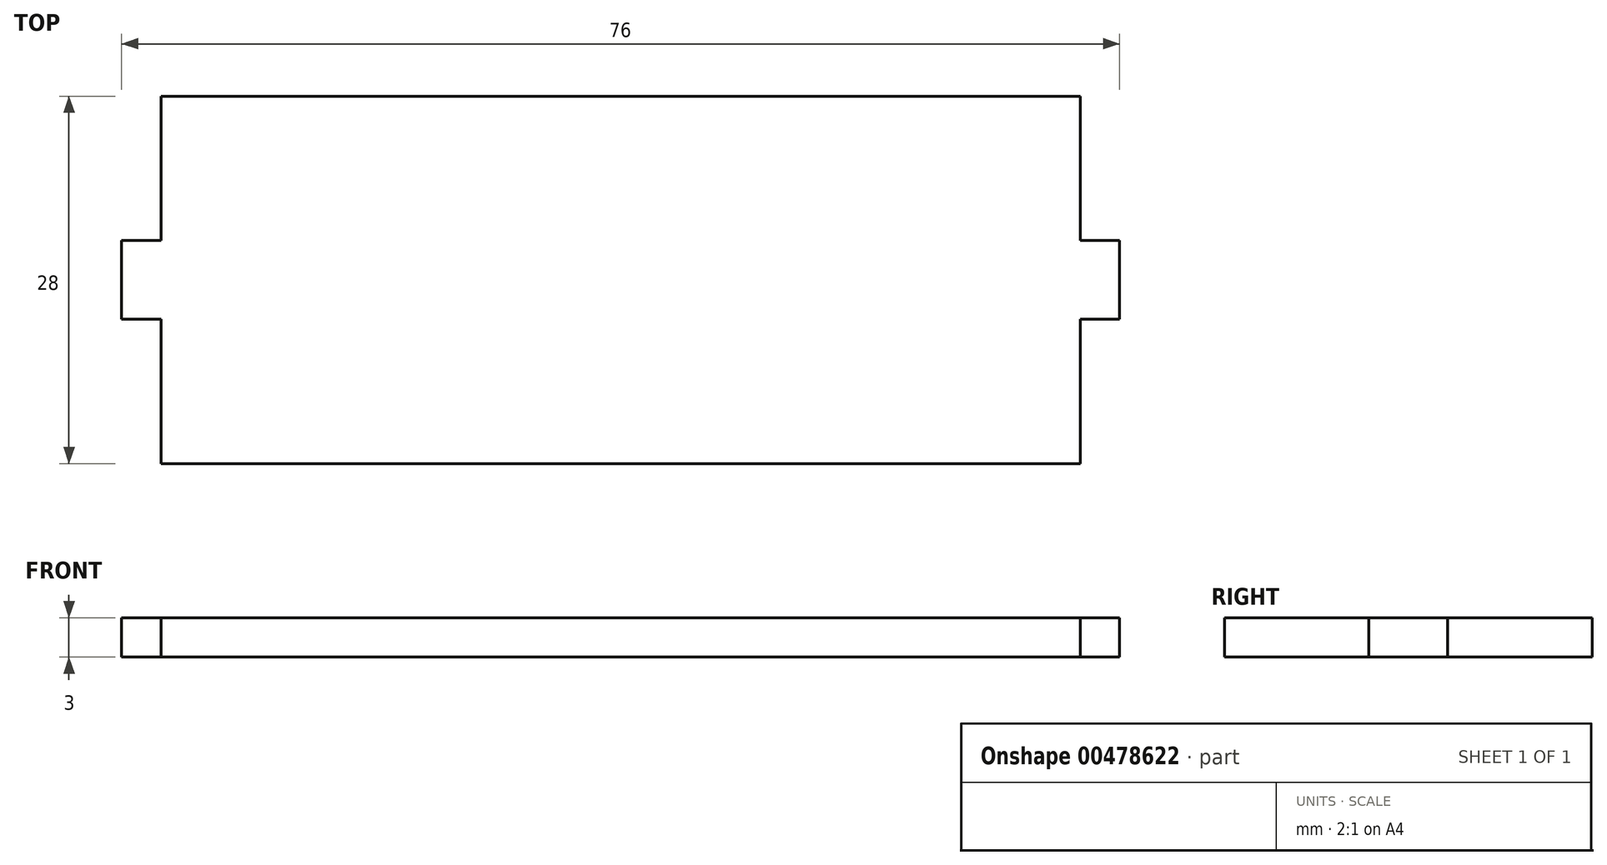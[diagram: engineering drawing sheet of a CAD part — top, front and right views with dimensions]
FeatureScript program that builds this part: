
annotation { "Feature Type Name" : "Feature", "Feature Type Description" : "" }
export const myFeature = defineFeature(function(context is Context, id is Id, definition is map)
    precondition{}
    {
        {
            var Q0;
            Q0=qCreatedBy(makeId("Top.planeOp"),FACE);
            var sketch = newSketch(context, id + "F0", { "sketchPlane" : qUnion([Q0])});
            skLineSegment(sketch, "E0.bottom", {"start": v(35, 14) * mm, "end": v(-35, 14) * mm});
            skLineSegment(sketch, "E0.top", {"start": v(35, -14) * mm, "end": v(-35, -14) * mm});
            skLineSegment(sketch, "E0.left", {"start": v(35, 14) * mm, "end": v(35, -14) * mm});
            skLineSegment(sketch, "E0.right", {"start": v(-35, 14) * mm, "end": v(-35, -14) * mm});
            skPoint(sketch, "E0.middle", {"position": v(0, 0) * mm});
            skSolve(sketch);
        }
        {
            var Q0;
            Q0 = qSketchRegion(id + "F0", true);
            extrude(context, id + "F1", {"entities" : qUnion([Q0]), "depth" : 3 * mm});
        }
        {
            var Q0;
            Q0=makeQuery(id+"F1.opExtrude","CAP_FACE",FACE,{"disambiguationData":[OSD([sQuery(id+"F0.wireOp",EDGE,"E0.bottom"),sQuery(id+"F0.wireOp",EDGE,"E0.top"),sQuery(id+"F0.wireOp",EDGE,"E0.left"),sQuery(id+"F0.wireOp",EDGE,"E0.right")])],"isStart":false});
            var sketch = newSketch(context, id + "F2", { "sketchPlane" : qUnion([Q0])});
            skLineSegment(sketch, "E1", {"start": v(-35, 0) * mm, "end": v(-38, 0) * mm, "construction": true});
            skPoint(sketch, "E1.endSnap0", {"position": v(-35, 0) * mm});
            skLineSegment(sketch, "E2.bottom", {"start": v(-35, 3) * mm, "end": v(-38, 3) * mm});
            skLineSegment(sketch, "E2.top", {"start": v(-35, -3) * mm, "end": v(-38, -3) * mm});
            skLineSegment(sketch, "E2.left", {"start": v(-35, 3) * mm, "end": v(-35, -3) * mm});
            skLineSegment(sketch, "E2.right", {"start": v(-38, 3) * mm, "end": v(-38, -3) * mm});
            skPoint(sketch, "E2.middle", {"position": v(-36.5, 0) * mm});
            skLineSegment(sketch, "E3", {"start": v(0, 14) * mm, "end": v(0, 6.14) * mm, "construction": true});
            skPoint(sketch, "E3.endSnap0", {"position": v(0, 14) * mm});
            skLineSegment(sketch, "E4.MirrorCS", {"start": v(35, 3) * mm, "end": v(38, 3) * mm});
            skLineSegment(sketch, "E5.MirrorCS", {"start": v(35, 3) * mm, "end": v(35, -3) * mm});
            skLineSegment(sketch, "E6.MirrorCS", {"start": v(38, 3) * mm, "end": v(38, -3) * mm});
            skLineSegment(sketch, "E7.MirrorCS", {"start": v(35, -3) * mm, "end": v(38, -3) * mm});
            skSolve(sketch);
        }
        {
            var Q0;
            Q0 = qSketchRegion(id + "F2", true);
            extrude(context, id + "F3", {"entities" : qUnion([Q0]), "operationType" : NewBodyOperationType.ADD, "oppositeDirection" : true, "depth" : 3 * mm});
        }
    });
